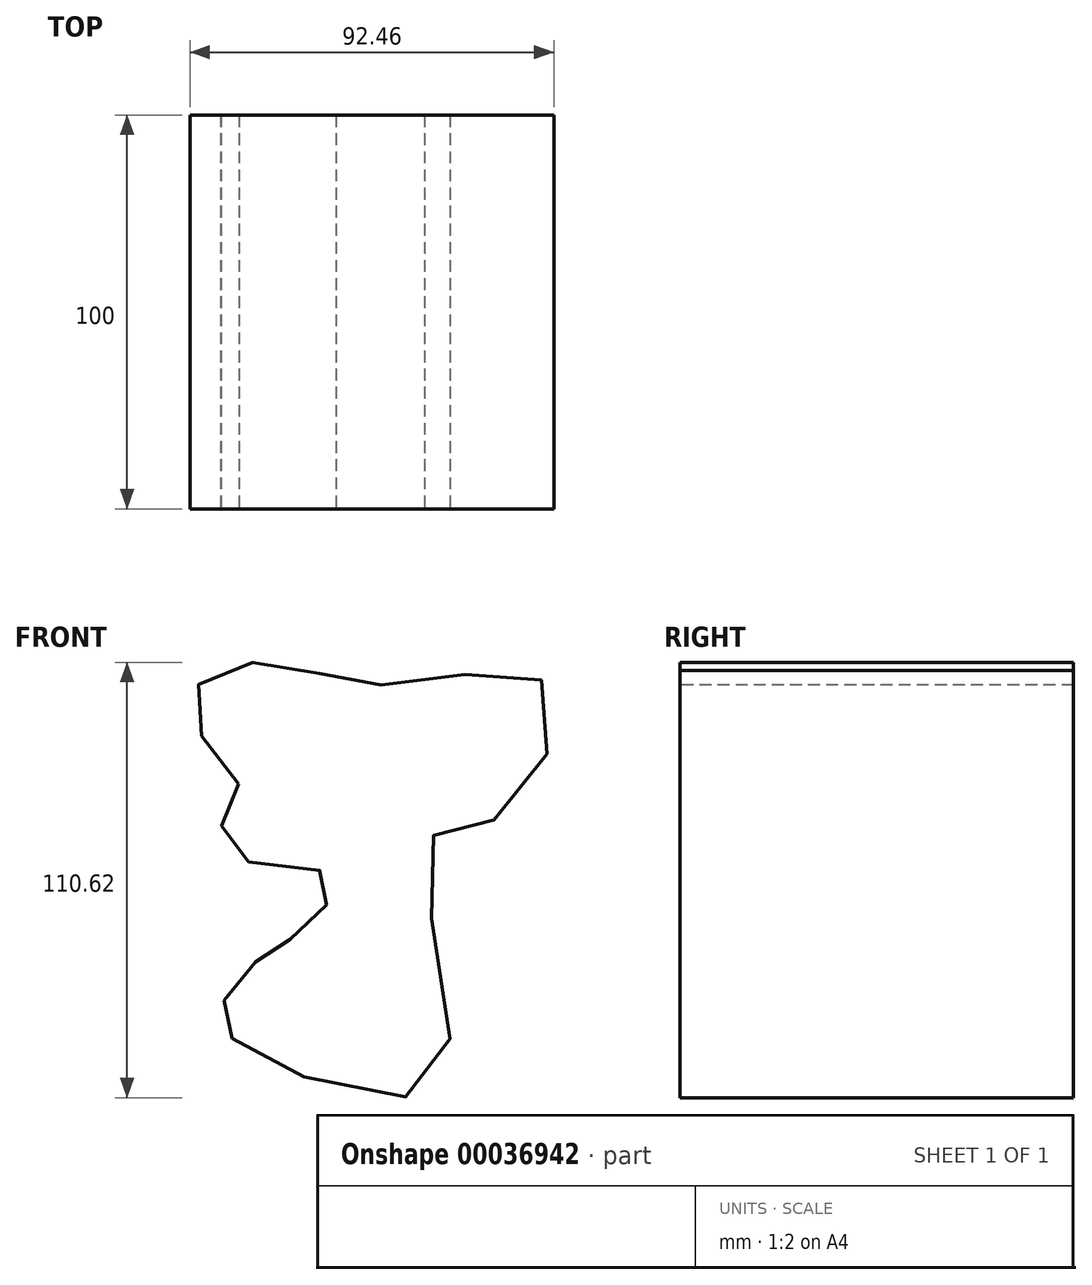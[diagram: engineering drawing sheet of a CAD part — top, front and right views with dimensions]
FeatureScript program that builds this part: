
annotation { "Feature Type Name" : "Feature", "Feature Type Description" : "" }
export const myFeature = defineFeature(function(context is Context, id is Id, definition is map)
    precondition{}
    {
        {
            var Q0;
            Q0=qCreatedBy(makeId("Front.planeOp"),FACE);
            var sketch = newSketch(context, id + "F0", { "sketchPlane" : qUnion([Q0])});
            skFitSpline(sketch, "E0", {"points": [v(-34.8, 40.93) * mm, v(-39.08, 30.38) * mm, v(-32.52, 21.25) * mm, v(-10.38, 17.06) * mm, v(-17.68, 4.42) * mm, v(-24.59, 0) * mm, v(-34.23, -7.84) * mm, v(-39.36, -18.11) * mm, v(-28.8, -28.67) * mm, v(16.51, -34) * mm, v(13.19, 25.83) * mm, v(33.13, 33.38) * mm, v(43.1, 66.32) * mm, v(7.7, 66.32) * mm, v(-15.69, 69.46) * mm, v(-39.65, 70.31) * mm, v(-46.78, 57.76) * mm, v(-34.8, 40.93) * mm]});
            skSolve(sketch);
        }
        {
            var Q0;
            Q0=sQuery(id+"F0.wireOp",EDGE,"E0");
            extrude(context, id + "F1", {"bodyType" : ToolBodyType.SURFACE, "surfaceEntities" : qUnion([Q0]), "depth" : 100 * mm});
        }
    });
